# Revit family: assa_abloy_sl500_r92_01
name_source: partatom
category: Doors
units: mm (PartAtom-declared; Revit-internal decimal feet)

## family parameters
Always vertical = Yes
Cut with Voids When Loaded = No
Host = Wall
OmniClass Number = 23.30.10.17.11
OmniClass Title = Sliding Doors
Room Calculation Point = No
Shared = No

## types (1)
- ERROR_LOAD TYPE CATALOG
    Analytic Construction = <None>
    Assembly Code = B2030110
    Description = Full Breakout, Bi-Parting, Medium Stile Door
    Door Configuration = FBO, Bi-Parting
    Door Construction Material = Powder Coat Custom
    Door Panel Fire Rating = none
    Door Panel Type = 1 Window
    ENGworks URL = www.ENGworksGlobal.com
    Frame Construction Material = Hollow Metal
    Frame Fire Rating = none
    Frame Material = Metal - ASSA ABLOY - Powder Coat Aluminum
    Manufacturer = ASSA ABLOY
    Maximum Door Height = 92 "
    Maximum Door Width = 192 "
    Minimum Door Height = 90 "
    Minimum Door Width = 96 "
    Part Description = See Description
    Part Number = See Series
    Product Documentation Link = https://www.assaabloyentrance.us
    Product Page URL = https://www.assaabloyentrance.us
    Series = SL500 R92 Windload
    URL = https://www.assaabloyentrance.us
    Version = 1
    Wall Closure = By host
    z Door Offset from Wall = 0 "
    z Door Panel Design = 1 Window
    z Door Panel Material = Powder Coat Custom
    z Door Panel Overlap When Closed = 5 "
    z Door Panel Overlap When Open = 8.156 "
    z Door Panel Thickness = 2.25 "
    z Door Panel Type = Generic Door Panel : Aluminum 1 Window Medium Stile
    z Fixed Sidelite = No
    z Frame Construction Material = Aluminum
    z Frame Height Head = 8 "
    z Frame Height Header = 8 "
    z Frame Height Sill = 0 "
    z Frame Overlap Bottom = 0 "
    z Frame Overlap Sides = 0 "
    z Frame Overlap Top = 0 "
    z Frame Projection = 0 "
    z Frame Projection Depth = 0.625 "
    z Frame Rabbet Height = 0.625 "
    z Frame Thickness = 4.5 "
    z Frame Thickness Matches Wall = No
    z Frame Width Center = 2.25 "
    z Frame Width Jambs = 1.75 "
    z Frame Width Legs = 3 "
    z Frame is Hollow = Yes
    z Full Breakout = Yes
    z Glass Thickness = 0.125 "
    z Operable Panel Count Left = 2
    z Operable Panel Count Right = 2
    z Rough Opening Gap Sides = 0.25 "
    z Rough Opening Gap Top = 0.25 "
    z Sidelite Width Left = 0 "
    z Sidelite Width Right = 0 "
    z Sill Height = 0 "
    z Transom Height = 0 "
    z Transom is Continuous = No

## geometry (parser evidence)
native form markers: Sweep x12
no freeform markers — native parametric forms only
